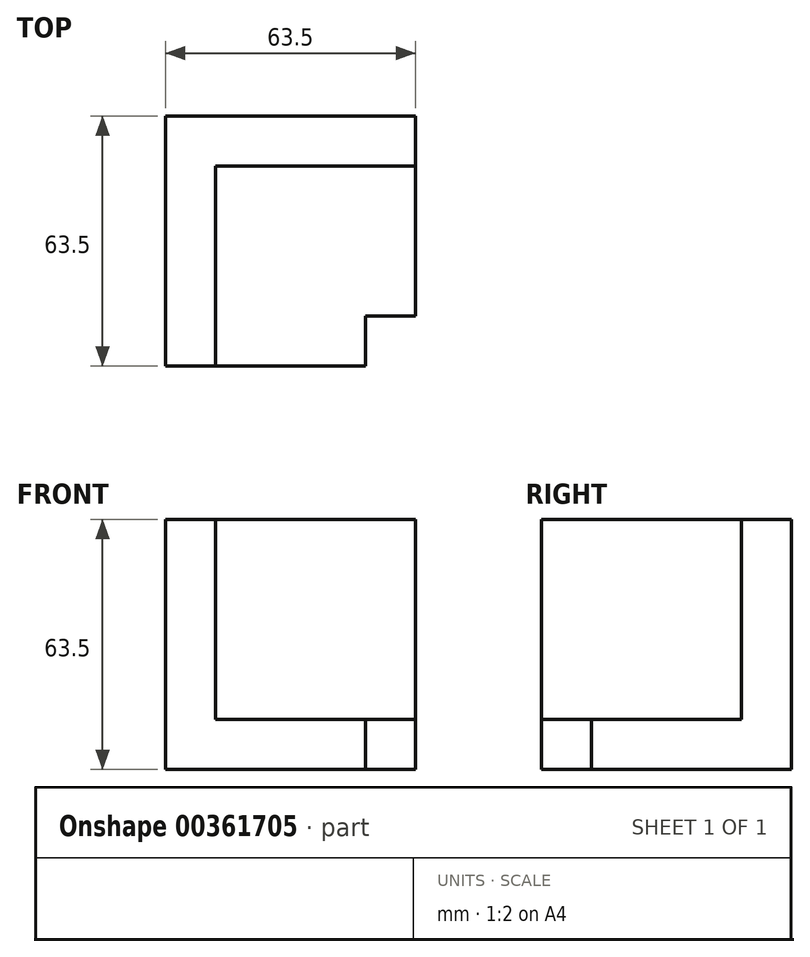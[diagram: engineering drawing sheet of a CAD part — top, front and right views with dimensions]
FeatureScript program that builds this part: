
annotation { "Feature Type Name" : "Feature", "Feature Type Description" : "" }
export const myFeature = defineFeature(function(context is Context, id is Id, definition is map)
    precondition{}
    {
        {
            var Q0;
            Q0=qCreatedBy(makeId("Front.planeOp"),FACE);
            var sketch = newSketch(context, id + "F0", { "sketchPlane" : qUnion([Q0])});
            skLineSegment(sketch, "E0.bottom", {"start": v(0, 0) * mm, "end": v(12.7, 0) * mm});
            skLineSegment(sketch, "E0.top", {"start": v(0, -63.5) * mm, "end": v(12.7, -63.5) * mm});
            skLineSegment(sketch, "E0.left", {"start": v(0, 0) * mm, "end": v(0, -63.5) * mm});
            skLineSegment(sketch, "E0.right", {"start": v(12.7, 0) * mm, "end": v(12.7, -63.5) * mm});
            skSolve(sketch);
        }
        {
            var Q0;
            Q0=makeQuery(id+"F0.imprint","IMPRINT",FACE,{"disambiguationData":[TD([[makeQuery(id+"F0.imprint","IMPRINT",EDGE,{"derivedFrom":sQuery(id+"F0.wireOp",EDGE,"E0.bottom")}),-1.0]])]});
            extrude(context, id + "F1", {"entities" : qUnion([Q0]), "depth" : 63.5 * mm});
        }
        {
            var Q0;
            Q0=makeQuery(id+"F1.opExtrude","SWEPT_FACE",FACE,{"disambiguationData":[OSD([sQuery(id+"F0.wireOp",EDGE,"E0.right")])]});
            var sketch = newSketch(context, id + "F2", { "sketchPlane" : qUnion([Q0])});
            skLineSegment(sketch, "E1.bottom", {"start": v(0, 0) * mm, "end": v(-12.7, 0) * mm});
            skLineSegment(sketch, "E1.top", {"start": v(0, -63.5) * mm, "end": v(-12.7, -63.5) * mm});
            skLineSegment(sketch, "E1.left", {"start": v(0, 0) * mm, "end": v(0, -63.5) * mm});
            skLineSegment(sketch, "E1.right", {"start": v(-12.7, 0) * mm, "end": v(-12.7, -63.5) * mm});
            skSolve(sketch);
        }
        {
            var Q0;
            Q0=makeQuery(id+"F2.imprint","IMPRINT",FACE,{"disambiguationData":[TD([[makeQuery(id+"F2.imprint","IMPRINT",EDGE,{"derivedFrom":sQuery(id+"F2.wireOp",EDGE,"E1.bottom")}),-1.0]])]});
            extrude(context, id + "F3", {"entities" : qUnion([Q0]), "operationType" : NewBodyOperationType.ADD, "depth" : 50.8 * mm});
        }
        {
            var Q0;
            Q0=makeQuery(id+"F1.opExtrude","SWEPT_FACE",FACE,{"disambiguationData":[OSD([sQuery(id+"F0.wireOp",EDGE,"E0.right")])]});
            var sketch = newSketch(context, id + "F4", { "sketchPlane" : qUnion([Q0])});
            skLineSegment(sketch, "E2.bottom", {"start": v(-63.5, -63.5) * mm, "end": v(-12.7, -63.5) * mm});
            skLineSegment(sketch, "E2.top", {"start": v(-63.5, -50.8) * mm, "end": v(-12.7, -50.8) * mm});
            skLineSegment(sketch, "E2.left", {"start": v(-63.5, -63.5) * mm, "end": v(-63.5, -50.8) * mm});
            skLineSegment(sketch, "E2.right", {"start": v(-12.7, -63.5) * mm, "end": v(-12.7, -50.8) * mm});
            skSolve(sketch);
        }
        {
            var Q0;
            Q0=makeQuery(id+"F4.imprint","IMPRINT",FACE,{"disambiguationData":[TD([[makeQuery(id+"F4.imprint","IMPRINT",EDGE,{"derivedFrom":sQuery(id+"F4.wireOp",EDGE,"E2.bottom")}),1.0]])]});
            extrude(context, id + "F5", {"entities" : qUnion([Q0]), "operationType" : NewBodyOperationType.ADD, "depth" : 38.1 * mm});
        }
        {
            var Q0;
            Q0=makeQuery(id+"F3.opExtrude","SWEPT_FACE",FACE,{"disambiguationData":[OSD([sQuery(id+"F2.wireOp",EDGE,"E1.right")])]});
            var sketch = newSketch(context, id + "F6", { "sketchPlane" : qUnion([Q0])});
            skLineSegment(sketch, "E3.bottom", {"start": v(63.5, -50.8) * mm, "end": v(50.8, -50.8) * mm});
            skLineSegment(sketch, "E3.top", {"start": v(63.5, -63.5) * mm, "end": v(50.8, -63.5) * mm});
            skLineSegment(sketch, "E3.left", {"start": v(63.5, -50.8) * mm, "end": v(63.5, -63.5) * mm});
            skLineSegment(sketch, "E3.right", {"start": v(50.8, -50.8) * mm, "end": v(50.8, -63.5) * mm});
            skSolve(sketch);
        }
        {
            var Q0;
            Q0=makeQuery(id+"F6.imprint","IMPRINT",FACE,{"disambiguationData":[TD([[makeQuery(id+"F6.imprint","IMPRINT",EDGE,{"derivedFrom":sQuery(id+"F6.wireOp",EDGE,"E3.bottom")}),1.0]])]});
            extrude(context, id + "F7", {"entities" : qUnion([Q0]), "operationType" : NewBodyOperationType.ADD, "depth" : 38.1 * mm});
        }
    });
